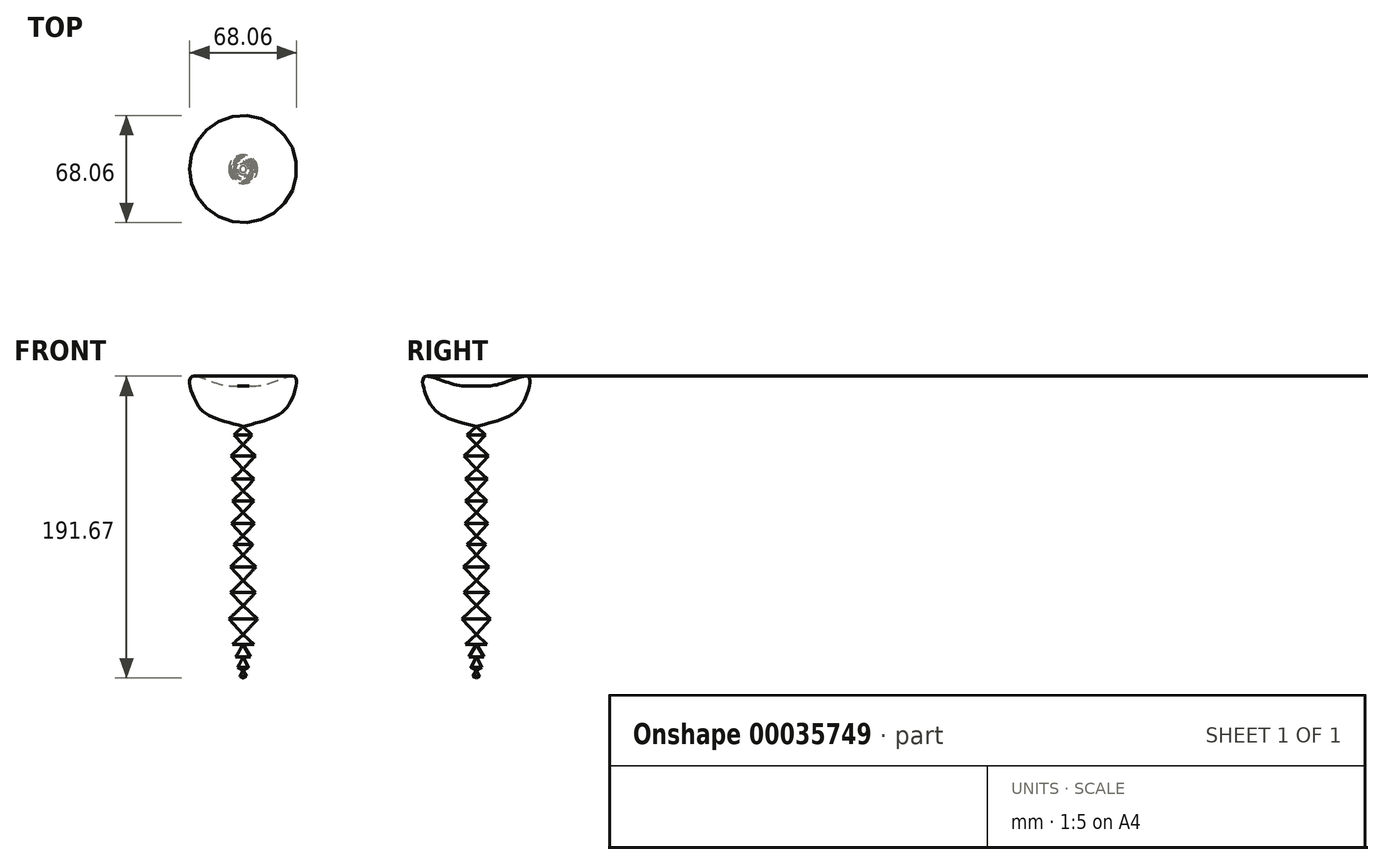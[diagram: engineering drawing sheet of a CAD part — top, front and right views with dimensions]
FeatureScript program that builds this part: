
annotation { "Feature Type Name" : "Feature", "Feature Type Description" : "" }
export const myFeature = defineFeature(function(context is Context, id is Id, definition is map)
    precondition{}
    {
        {
            var Q0;
            Q0=qCreatedBy(makeId("Front.planeOp"),FACE);
            var sketch = newSketch(context, id + "F0", { "sketchPlane" : qUnion([Q0])});
            skLineSegment(sketch, "E0", {"start": v(0, 18.79) * mm, "end": v(-5.77, 13.4) * mm});
            skLineSegment(sketch, "E1", {"start": v(-5.77, 13.4) * mm, "end": v(0, 7.22) * mm});
            skLineSegment(sketch, "E2", {"start": v(0, 7.22) * mm, "end": v(-7.72, 0) * mm});
            skLineSegment(sketch, "E3", {"start": v(-7.72, 0) * mm, "end": v(0, -8.25) * mm});
            skLineSegment(sketch, "E4", {"start": v(0, -8.25) * mm, "end": v(-6.98, -14.78) * mm});
            skLineSegment(sketch, "E5", {"start": v(-6.98, -14.78) * mm, "end": v(0, -22.23) * mm});
            skLineSegment(sketch, "E6", {"start": v(0, -22.23) * mm, "end": v(-6.89, -28.68) * mm});
            skLineSegment(sketch, "E7", {"start": v(-6.89, -28.68) * mm, "end": v(0, -36.04) * mm});
            skLineSegment(sketch, "E8", {"start": v(0, -36.04) * mm, "end": v(-7.33, -42.9) * mm});
            skLineSegment(sketch, "E9", {"start": v(-7.33, -42.9) * mm, "end": v(0, -50.73) * mm});
            skLineSegment(sketch, "E10", {"start": v(0, -50.73) * mm, "end": v(-6.07, -56.4) * mm});
            skLineSegment(sketch, "E11", {"start": v(-6.07, -56.4) * mm, "end": v(0, -62.9) * mm});
            skLineSegment(sketch, "E12", {"start": v(0, -62.9) * mm, "end": v(-8.15, -70.51) * mm});
            skLineSegment(sketch, "E13", {"start": v(-8.15, -70.51) * mm, "end": v(0, -79.23) * mm});
            skLineSegment(sketch, "E14", {"start": v(0, -79.23) * mm, "end": v(-7.94, -86.66) * mm});
            skLineSegment(sketch, "E15", {"start": v(-7.94, -86.66) * mm, "end": v(0, -95.15) * mm});
            skLineSegment(sketch, "E16", {"start": v(0, -95.15) * mm, "end": v(-9.12, -103.68) * mm});
            skLineSegment(sketch, "E17", {"start": v(-9.12, -103.68) * mm, "end": v(0, -113.44) * mm});
            skLineSegment(sketch, "E18", {"start": v(0, -113.44) * mm, "end": v(-6.77, -119.77) * mm});
            skLineSegment(sketch, "E19", {"start": v(-6.77, -119.77) * mm, "end": v(0, -119.77) * mm});
            skLineSegment(sketch, "E20", {"start": v(0, -119.77) * mm, "end": v(-4.73, -127.77) * mm});
            skLineSegment(sketch, "E21", {"start": v(-4.73, -127.77) * mm, "end": v(0, -127.77) * mm});
            skLineSegment(sketch, "E22", {"start": v(0, -127.77) * mm, "end": v(-3.48, -134.35) * mm});
            skLineSegment(sketch, "E23", {"start": v(-3.48, -134.35) * mm, "end": v(0, -136.2) * mm});
            skLineSegment(sketch, "E24", {"start": v(0, -136.2) * mm, "end": v(-2.01, -140) * mm});
            skLineSegment(sketch, "E25", {"start": v(-2.01, -140) * mm, "end": v(0, -141.07) * mm});
            skLineSegment(sketch, "E26", {"start": v(0, -162.87) * mm, "end": v(0, 69.57) * mm});
            skFitSpline(sketch, "E27", {"points": [v(0, 18.79) * mm, v(-23.46, 26.82) * mm, v(-31.76, 38.19) * mm, v(-33.02, 50.1) * mm, v(-16.06, 45.95) * mm, v(0, 44.33) * mm], "startDerivative": vector(-110.18, 26.72) * mm, "endDerivative": vector(74.75, 1.92) * mm});
            skSolve(sketch);
        }
        {
            var Q0;
            {var subQ2=sQuery(id+"F0.wireOp",EDGE,"E14");Q0=makeQuery(id+"F0.imprint","IMPRINT",FACE,{"disambiguationData":[TD([[makeQuery(id+"F0.imprint","IMPRINT",EDGE,{"derivedFrom":subQ2}),1.0]])]});}
            var Q1;
            {var subQ2=sQuery(id+"F0.wireOp",EDGE,"E0");Q1=makeQuery(id+"F0.imprint","IMPRINT",FACE,{"disambiguationData":[TD([[makeQuery(id+"F0.imprint","IMPRINT",EDGE,{"derivedFrom":subQ2}),1.0]])]});}
            var Q2;
            {var subQ2=sQuery(id+"F0.wireOp",EDGE,"E22");Q2=makeQuery(id+"F0.imprint","IMPRINT",FACE,{"disambiguationData":[TD([[makeQuery(id+"F0.imprint","IMPRINT",EDGE,{"derivedFrom":subQ2}),1.0]])]});}
            var Q3;
            {var subQ2=sQuery(id+"F0.wireOp",EDGE,"E12");Q3=makeQuery(id+"F0.imprint","IMPRINT",FACE,{"disambiguationData":[TD([[makeQuery(id+"F0.imprint","IMPRINT",EDGE,{"derivedFrom":subQ2}),1.0]])]});}
            var Q4;
            {var subQ2=sQuery(id+"F0.wireOp",EDGE,"E4");Q4=makeQuery(id+"F0.imprint","IMPRINT",FACE,{"disambiguationData":[TD([[makeQuery(id+"F0.imprint","IMPRINT",EDGE,{"derivedFrom":subQ2}),1.0]])]});}
            var Q5;
            {var subQ2=sQuery(id+"F0.wireOp",EDGE,"E6");Q5=makeQuery(id+"F0.imprint","IMPRINT",FACE,{"disambiguationData":[TD([[makeQuery(id+"F0.imprint","IMPRINT",EDGE,{"derivedFrom":subQ2}),1.0]])]});}
            var Q6;
            {var subQ2=sQuery(id+"F0.wireOp",EDGE,"E8");Q6=makeQuery(id+"F0.imprint","IMPRINT",FACE,{"disambiguationData":[TD([[makeQuery(id+"F0.imprint","IMPRINT",EDGE,{"derivedFrom":subQ2}),1.0]])]});}
            var Q7;
            {var subQ2=sQuery(id+"F0.wireOp",EDGE,"E10");Q7=makeQuery(id+"F0.imprint","IMPRINT",FACE,{"disambiguationData":[TD([[makeQuery(id+"F0.imprint","IMPRINT",EDGE,{"derivedFrom":subQ2}),1.0]])]});}
            var Q8;
            {var subQ2=sQuery(id+"F0.wireOp",EDGE,"E18");Q8=makeQuery(id+"F0.imprint","IMPRINT",FACE,{"disambiguationData":[TD([[makeQuery(id+"F0.imprint","IMPRINT",EDGE,{"derivedFrom":subQ2}),1.0]])]});}
            var Q9;
            {var subQ2=sQuery(id+"F0.wireOp",EDGE,"E24");Q9=makeQuery(id+"F0.imprint","IMPRINT",FACE,{"disambiguationData":[TD([[makeQuery(id+"F0.imprint","IMPRINT",EDGE,{"derivedFrom":subQ2}),1.0]])]});}
            var Q10;
            {var subQ2=sQuery(id+"F0.wireOp",EDGE,"E16");Q10=makeQuery(id+"F0.imprint","IMPRINT",FACE,{"disambiguationData":[TD([[makeQuery(id+"F0.imprint","IMPRINT",EDGE,{"derivedFrom":subQ2}),1.0]])]});}
            var Q11;
            {var subQ2=sQuery(id+"F0.wireOp",EDGE,"E2");Q11=makeQuery(id+"F0.imprint","IMPRINT",FACE,{"disambiguationData":[TD([[makeQuery(id+"F0.imprint","IMPRINT",EDGE,{"derivedFrom":subQ2}),1.0]])]});}
            var Q12;
            {var subQ2=sQuery(id+"F0.wireOp",EDGE,"E20");Q12=makeQuery(id+"F0.imprint","IMPRINT",FACE,{"disambiguationData":[TD([[makeQuery(id+"F0.imprint","IMPRINT",EDGE,{"derivedFrom":subQ2}),1.0]])]});}
            var Q13;
            {var subQ0=sQuery(id+"F0.wireOp",EDGE,"E27");Q13=makeQuery(id+"F0.imprint","IMPRINT",FACE,{"disambiguationData":[TD([[makeQuery(id+"F0.imprint","IMPRINT",EDGE,{"derivedFrom":subQ0}),-1.0]])]});}
            var Q14;
            Q14=sQuery(id+"F0.wireOp",EDGE,"E26");
            revolve(context, id + "F1", {"entities" : qUnion([Q0, Q1, Q2, Q3, Q4, Q5, Q6, Q7, Q8, Q9, Q10, Q11, Q12, Q13]), "axis" : qUnion([Q14]), "revolveType" : RevolveType.FULL});
        }
    });
